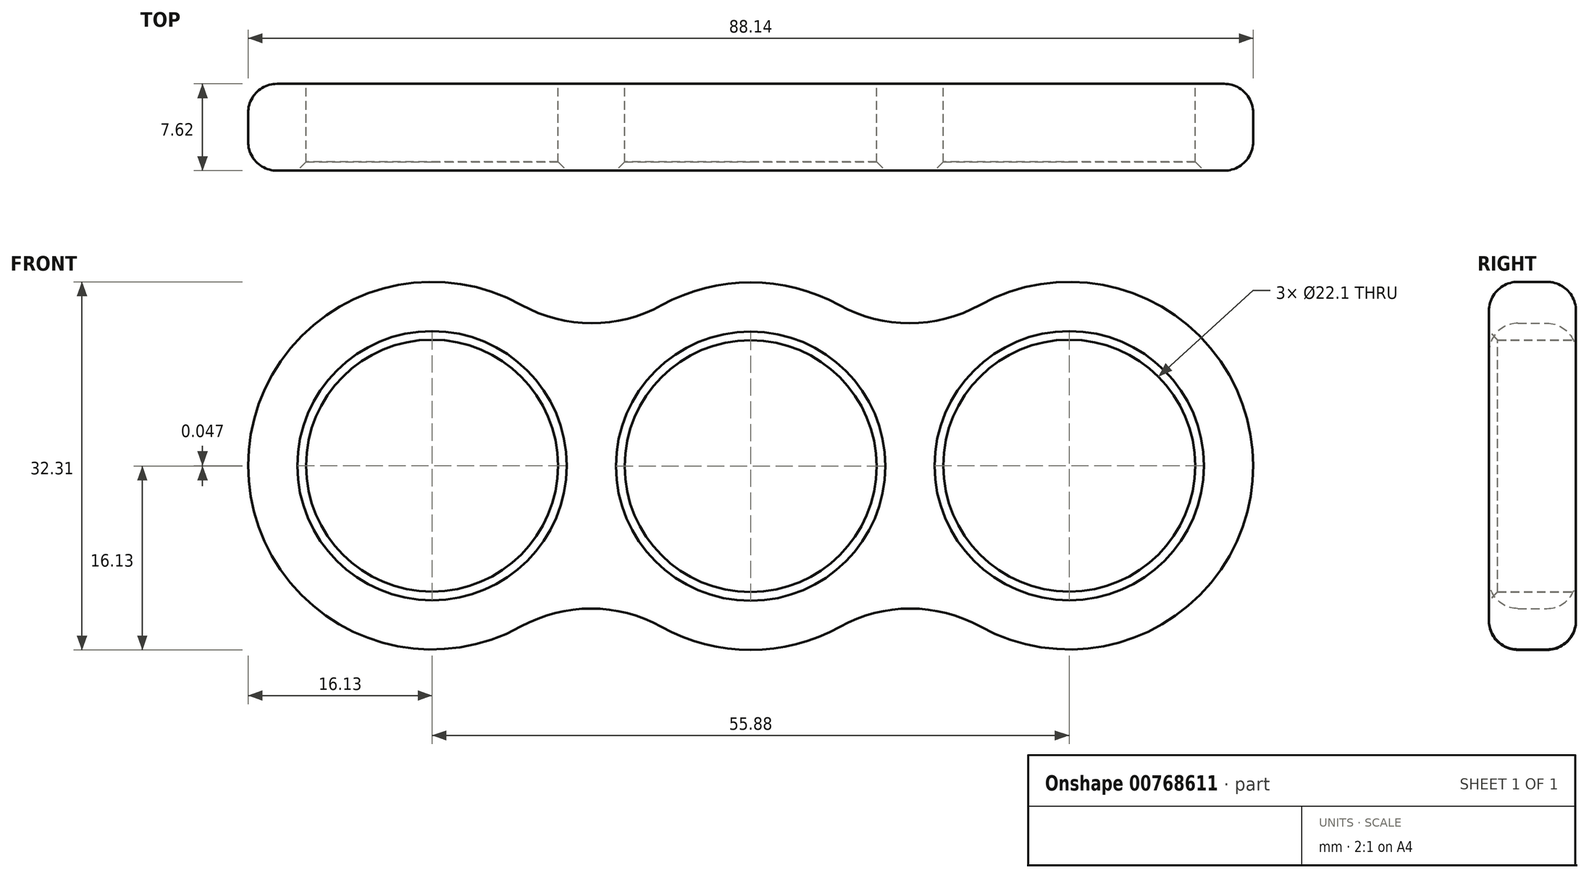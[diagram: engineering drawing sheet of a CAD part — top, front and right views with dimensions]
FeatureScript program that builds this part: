
annotation { "Feature Type Name" : "Feature", "Feature Type Description" : "" }
export const myFeature = defineFeature(function(context is Context, id is Id, definition is map)
    precondition{}
    {
        {
            var Q0;
            Q0=qCreatedBy(makeId("Front.planeOp"),FACE);
            var sketch = newSketch(context, id + "F0", { "sketchPlane" : qUnion([Q0])});
            skCircle(sketch, "E0", {"center": v(0, 0) * mm, "radius": 11.05 * mm});
            skCircle(sketch, "E1", {"center": v(27.94, 0.05) * mm, "radius": 11.05 * mm});
            skCircle(sketch, "E2.MirrorC", {"center": v(-27.94, 0.05) * mm, "radius": 11.05 * mm});
            skArc(sketch, "E3.0", {"start": v(-7.84, -14.1) * mm, "mid": v(0, -16.13) * mm, "end": v(7.84, -14.1) * mm});
            skArc(sketch, "E4.0", {"start": v(20.15, -14.07) * mm, "mid": v(44.07, 0.07) * mm, "end": v(20.1, 14.14) * mm});
            skArc(sketch, "E5.0", {"start": v(-20.15, -14.07) * mm, "mid": v(-44.07, 0.07) * mm, "end": v(-20.1, 14.14) * mm});
            skArc(sketch, "E6.trimOffspring", {"start": v(7.8, 14.12) * mm, "mid": v(0, 16.13) * mm, "end": v(-7.8, 14.12) * mm});
            skPoint(sketch, "E7.visualSharp", {"position": v(-13.96, 8.08) * mm});
            skArc(sketch, "E7.filletArc", {"start": v(-20.1, 14.14) * mm, "mid": v(-13.95, 12.54) * mm, "end": v(-7.8, 14.12) * mm});
            skPoint(sketch, "E8.visualSharp", {"position": v(13.96, 8.08) * mm});
            skArc(sketch, "E8.filletArc", {"start": v(7.8, 14.12) * mm, "mid": v(13.95, 12.54) * mm, "end": v(20.1, 14.14) * mm});
            skPoint(sketch, "E9.visualSharp", {"position": v(13.98, -8.04) * mm});
            skArc(sketch, "E9.filletArc", {"start": v(20.15, -14.07) * mm, "mid": v(14, -12.5) * mm, "end": v(7.84, -14.1) * mm});
            skPoint(sketch, "E10.visualSharp", {"position": v(-13.98, -8.04) * mm});
            skArc(sketch, "E10.filletArc", {"start": v(-7.84, -14.1) * mm, "mid": v(-14, -12.5) * mm, "end": v(-20.15, -14.07) * mm});
            skSolve(sketch);
        }
        {
            var Q0;
            Q0=makeQuery(id+"F0.imprint","IMPRINT",FACE,{"disambiguationData":[TD([[makeQuery(id+"F0.imprint","IMPRINT",EDGE,{"derivedFrom":sQuery(id+"F0.wireOp",EDGE,"E0")}),-1.0]])]});
            extrude(context, id + "F1", {"entities" : qUnion([Q0]), "depth" : 7.62 * mm, "offsetDistance" : 25.4 * mm});
        }
        {
            var Q0;
            Q0=makeQuery(id+"F1.opExtrude","CAP_EDGE",EDGE,{"disambiguationData":[OSD([sQuery(id+"F0.wireOp",EDGE,"E4.0")])],"isStart":false});
            var Q1;
            Q1=makeQuery(id+"F1.opExtrude","CAP_EDGE",EDGE,{"disambiguationData":[OSD([sQuery(id+"F0.wireOp",EDGE,"E4.0")])],"isStart":true});
            fillet(context, id + "F2", {"entities" : qUnion([Q0, Q1]), "radius" : 2.54 * mm, "tangentPropagation" : true, "allowEdgeOverflow" : false});
        }
        {
            var Q0;
            Q0=makeQuery(id+"F1.opExtrude","CAP_EDGE",EDGE,{"disambiguationData":[OSD([sQuery(id+"F0.wireOp",EDGE,"E2.MirrorC")])],"isStart":false});
            var Q1;
            Q1=makeQuery(id+"F1.opExtrude","CAP_EDGE",EDGE,{"disambiguationData":[OSD([sQuery(id+"F0.wireOp",EDGE,"E0")])],"isStart":false});
            var Q2;
            Q2=makeQuery(id+"F1.opExtrude","CAP_EDGE",EDGE,{"disambiguationData":[OSD([sQuery(id+"F0.wireOp",EDGE,"E1")])],"isStart":false});
            chamfer(context, id + "F3", {"entities" : qUnion([Q0, Q1, Q2]), "width" : 0.76 * mm, "tangentPropagation" : true});
        }
    });
